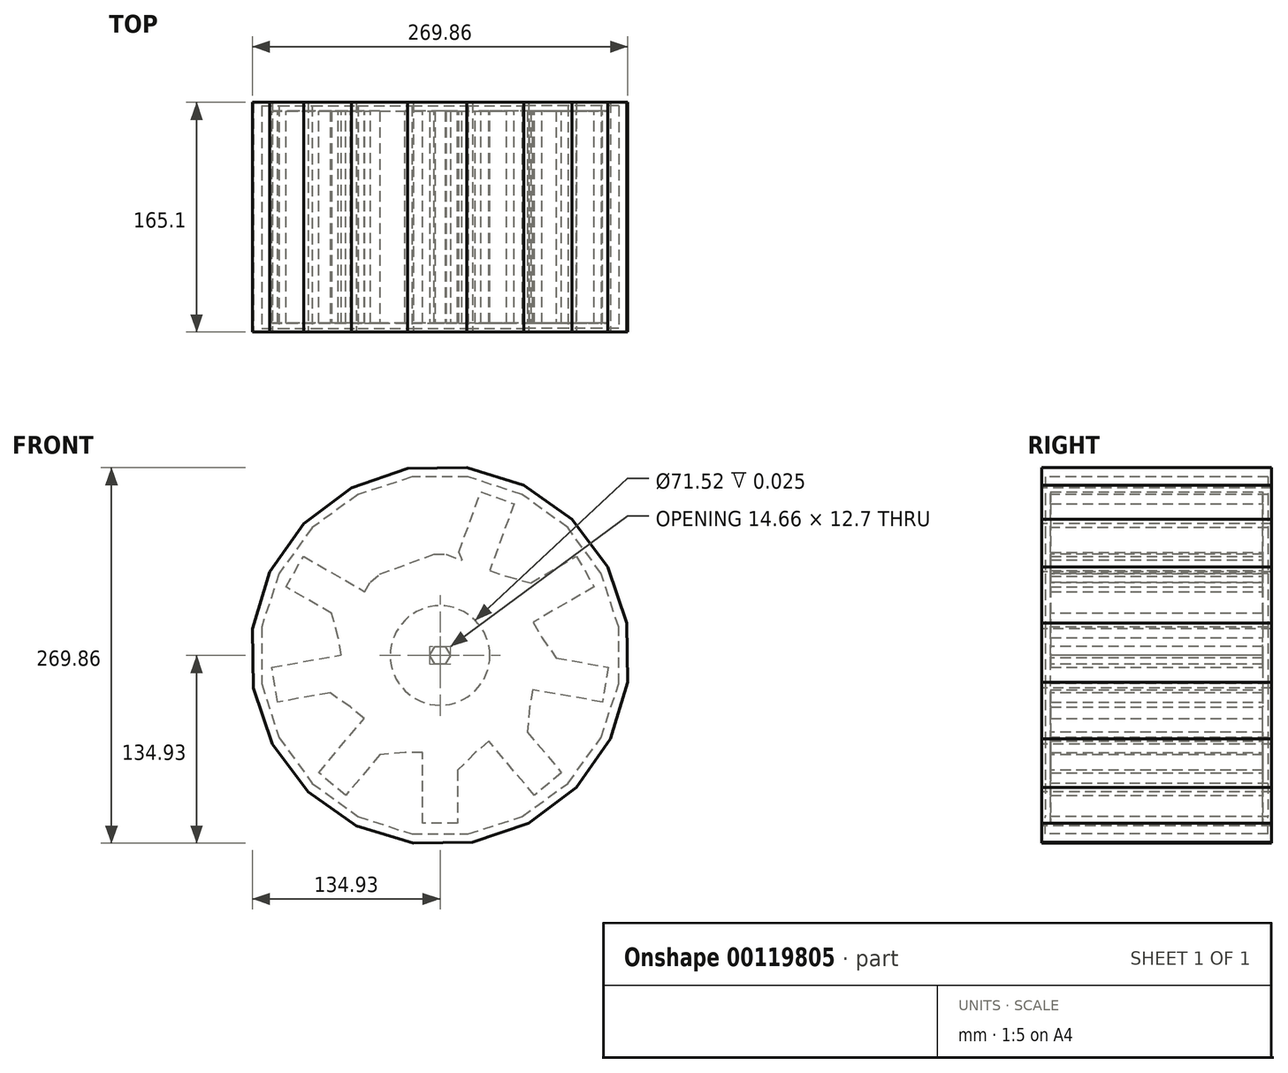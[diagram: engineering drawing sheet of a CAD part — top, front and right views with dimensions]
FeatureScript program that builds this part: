
annotation { "Feature Type Name" : "Feature", "Feature Type Description" : "" }
export const myFeature = defineFeature(function(context is Context, id is Id, definition is map)
    precondition{}
    {
        {
            var Q0;
            Q0=qCreatedBy(makeId("Front.planeOp"),FACE);
            var sketch = newSketch(context, id + "F0", { "sketchPlane" : qUnion([Q0])});
            skCircle(sketch, "E0.cCircle", {"center": v(0, 0) * mm, "radius": 69.79 * mm, "construction": true});
            skLineSegment(sketch, "E0.0", {"start": v(25.4, -69.79) * mm, "end": v(-25.4, -69.79) * mm});
            skLineSegment(sketch, "E0.1", {"start": v(-25.4, -69.79) * mm, "end": v(-64.32, -37.13) * mm});
            skLineSegment(sketch, "E0.2", {"start": v(-64.32, -37.13) * mm, "end": v(-73.14, 12.9) * mm});
            skLineSegment(sketch, "E0.3", {"start": v(-73.14, 12.9) * mm, "end": v(-47.74, 56.9) * mm});
            skLineSegment(sketch, "E0.4", {"start": v(-47.74, 56.9) * mm, "end": v(0, 74.26) * mm});
            skLineSegment(sketch, "E0.5", {"start": v(0, 74.26) * mm, "end": v(47.74, 56.9) * mm});
            skLineSegment(sketch, "E0.6", {"start": v(47.74, 56.9) * mm, "end": v(73.14, 12.9) * mm});
            skLineSegment(sketch, "E0.7", {"start": v(73.14, 12.9) * mm, "end": v(64.32, -37.13) * mm});
            skLineSegment(sketch, "E0.8", {"start": v(64.32, -37.13) * mm, "end": v(25.4, -69.79) * mm});
            skPoint(sketch, "E0.0.midPoint", {"position": v(0, -69.79) * mm});
            skLineSegment(sketch, "E1", {"start": v(-66.79, 23.9) * mm, "end": v(-110.78, 49.3) * mm});
            skLineSegment(sketch, "E2", {"start": v(-110.78, 49.3) * mm, "end": v(-98.08, 71.3) * mm});
            skLineSegment(sketch, "E3", {"start": v(-98.08, 71.3) * mm, "end": v(-54.09, 45.9) * mm});
            skLineSegment(sketch, "E4", {"start": v(-11.93, 69.92) * mm, "end": v(-29.3, 117.66) * mm});
            skLineSegment(sketch, "E5", {"start": v(-29.3, 117.66) * mm, "end": v(-5.44, 126.34) * mm});
            skLineSegment(sketch, "E6", {"start": v(-5.44, 126.34) * mm, "end": v(15.8, 67.97) * mm});
            skLineSegment(sketch, "E7.1.0", {"start": v(-120.96, -8.43) * mm, "end": v(-70.93, 0.39) * mm});
            skLineSegment(sketch, "E7.1.1", {"start": v(-66.52, -24.63) * mm, "end": v(-116.55, -33.45) * mm});
            skLineSegment(sketch, "E7.1.2", {"start": v(-116.55, -33.45) * mm, "end": v(-120.96, -8.43) * mm});
            skLineSegment(sketch, "E7.2.0", {"start": v(-87.24, -84.21) * mm, "end": v(-54.59, -45.3) * mm});
            skLineSegment(sketch, "E7.2.1", {"start": v(-35.13, -61.62) * mm, "end": v(-67.78, -100.54) * mm});
            skLineSegment(sketch, "E7.2.2", {"start": v(-67.78, -100.54) * mm, "end": v(-87.24, -84.21) * mm});
            skLineSegment(sketch, "E7.3.0", {"start": v(-12.7, -120.59) * mm, "end": v(-12.7, -69.79) * mm});
            skLineSegment(sketch, "E7.3.1", {"start": v(12.7, -69.79) * mm, "end": v(12.7, -120.59) * mm});
            skLineSegment(sketch, "E7.3.2", {"start": v(12.7, -120.59) * mm, "end": v(-12.7, -120.59) * mm});
            skLineSegment(sketch, "E7.4.0", {"start": v(67.78, -100.54) * mm, "end": v(35.13, -61.62) * mm});
            skLineSegment(sketch, "E7.4.1", {"start": v(54.59, -45.3) * mm, "end": v(87.24, -84.21) * mm});
            skLineSegment(sketch, "E7.4.2", {"start": v(87.24, -84.21) * mm, "end": v(67.78, -100.54) * mm});
            skLineSegment(sketch, "E7.5.0", {"start": v(116.55, -33.45) * mm, "end": v(66.52, -24.63) * mm});
            skLineSegment(sketch, "E7.5.1", {"start": v(70.93, 0.39) * mm, "end": v(120.96, -8.43) * mm});
            skLineSegment(sketch, "E7.5.2", {"start": v(120.96, -8.43) * mm, "end": v(116.55, -33.45) * mm});
            skLineSegment(sketch, "E7.6.0", {"start": v(110.78, 49.3) * mm, "end": v(66.79, 23.9) * mm});
            skLineSegment(sketch, "E7.6.1", {"start": v(54.09, 45.9) * mm, "end": v(98.08, 71.3) * mm});
            skLineSegment(sketch, "E7.6.2", {"start": v(98.08, 71.3) * mm, "end": v(110.78, 49.3) * mm});
            skLineSegment(sketch, "E7.7.0", {"start": v(53.18, 108.97) * mm, "end": v(35.8, 61.23) * mm});
            skLineSegment(sketch, "E7.7.1", {"start": v(11.93, 69.92) * mm, "end": v(29.3, 117.66) * mm});
            skLineSegment(sketch, "E7.7.2", {"start": v(29.3, 117.66) * mm, "end": v(53.18, 108.97) * mm});
            skLineSegment(sketch, "E7.8.0", {"start": v(-29.3, 117.66) * mm, "end": v(-11.93, 69.92) * mm});
            skLineSegment(sketch, "E7.8.1", {"start": v(-35.8, 61.23) * mm, "end": v(-53.18, 108.97) * mm});
            skLineSegment(sketch, "E7.8.2", {"start": v(-53.18, 108.97) * mm, "end": v(-29.3, 117.66) * mm});
            skSolve(sketch);
        }
        {
            var Q0;
            {var subQ20=sQuery(id+"F0.wireOp",EDGE,"E0.8");var subQ23=sQuery(id+"F0.wireOp",EDGE,"E0.0");var subQ33=makeQuery(id+"F0.imprint","INTERSECT",VERTEX,{"derivedFrom":[subQ23,subQ20]});Q0=makeQuery(id+"F0.imprint","IMPRINT",FACE,{"disambiguationData":[TD([[makeQuery(id+"F0.imprint","IMPRINT",EDGE,{"disambiguationData":[TD([[subQ33,-1.0]])],"derivedFrom":subQ23}),-1.0]])]});}
            var Q1;
            {var subQ0=sQuery(id+"F0.wireOp",EDGE,"E1");Q1=makeQuery(id+"F0.imprint","IMPRINT",FACE,{"disambiguationData":[TD([[makeQuery(id+"F0.imprint","IMPRINT",EDGE,{"derivedFrom":subQ0}),-1.0]])]});}
            var Q2;
            {var subQ0=sQuery(id+"F0.wireOp",EDGE,"E7.8.0");Q2=makeQuery(id+"F0.imprint","IMPRINT",FACE,{"disambiguationData":[TD([[makeQuery(id+"F0.imprint","IMPRINT",EDGE,{"derivedFrom":subQ0}),-1.0]])]});}
            var Q3;
            {var subQ0=sQuery(id+"F0.wireOp",EDGE,"E7.7.0");Q3=makeQuery(id+"F0.imprint","IMPRINT",FACE,{"disambiguationData":[TD([[makeQuery(id+"F0.imprint","IMPRINT",EDGE,{"derivedFrom":subQ0}),-1.0]])]});}
            var Q4;
            {var subQ0=sQuery(id+"F0.wireOp",EDGE,"E7.6.0");Q4=makeQuery(id+"F0.imprint","IMPRINT",FACE,{"disambiguationData":[TD([[makeQuery(id+"F0.imprint","IMPRINT",EDGE,{"derivedFrom":subQ0}),-1.0]])]});}
            var Q5;
            {var subQ0=sQuery(id+"F0.wireOp",EDGE,"E7.5.0");Q5=makeQuery(id+"F0.imprint","IMPRINT",FACE,{"disambiguationData":[TD([[makeQuery(id+"F0.imprint","IMPRINT",EDGE,{"derivedFrom":subQ0}),-1.0]])]});}
            var Q6;
            {var subQ0=sQuery(id+"F0.wireOp",EDGE,"E7.4.0");Q6=makeQuery(id+"F0.imprint","IMPRINT",FACE,{"disambiguationData":[TD([[makeQuery(id+"F0.imprint","IMPRINT",EDGE,{"derivedFrom":subQ0}),-1.0]])]});}
            var Q7;
            {var subQ0=sQuery(id+"F0.wireOp",EDGE,"E7.3.0");Q7=makeQuery(id+"F0.imprint","IMPRINT",FACE,{"disambiguationData":[TD([[makeQuery(id+"F0.imprint","IMPRINT",EDGE,{"derivedFrom":subQ0}),-1.0]])]});}
            var Q8;
            {var subQ0=sQuery(id+"F0.wireOp",EDGE,"E7.2.0");Q8=makeQuery(id+"F0.imprint","IMPRINT",FACE,{"disambiguationData":[TD([[makeQuery(id+"F0.imprint","IMPRINT",EDGE,{"derivedFrom":subQ0}),-1.0]])]});}
            var Q9;
            {var subQ0=sQuery(id+"F0.wireOp",EDGE,"E7.1.0");Q9=makeQuery(id+"F0.imprint","IMPRINT",FACE,{"disambiguationData":[TD([[makeQuery(id+"F0.imprint","IMPRINT",EDGE,{"derivedFrom":subQ0}),-1.0]])]});}
            extrude(context, id + "F1", {"entities" : qUnion([Q0, Q1, Q2, Q3, Q4, Q5, Q6, Q7, Q8, Q9]), "depth" : 152.4 * mm});
        }
        {
            var Q0;
            Q0=makeQuery(id+"F1.opExtrude","SWEPT_EDGE",EDGE,{"disambiguationData":[OSD([sQuery(id+"F0.wireOp",EDGE,"E0.6"),sQuery(id+"F0.wireOp",EDGE,"E7.6.1")])]});
            var Q1;
            Q1=makeQuery(id+"F1.opExtrude","SWEPT_EDGE",EDGE,{"disambiguationData":[OSD([sQuery(id+"F0.wireOp",EDGE,"E0.0"),sQuery(id+"F0.wireOp",EDGE,"E7.3.1")])]});
            var Q2;
            Q2=makeQuery(id+"F1.opExtrude","SWEPT_EDGE",EDGE,{"disambiguationData":[OSD([sQuery(id+"F0.wireOp",EDGE,"E0.3"),sQuery(id+"F0.wireOp",EDGE,"E1")])]});
            var Q3;
            Q3=makeQuery(id+"F1.opExtrude","SWEPT_EDGE",EDGE,{"disambiguationData":[OSD([sQuery(id+"F0.wireOp",EDGE,"E0.8"),sQuery(id+"F0.wireOp",EDGE,"E7.4.1")])]});
            var Q4;
            Q4=makeQuery(id+"F1.opExtrude","SWEPT_EDGE",EDGE,{"disambiguationData":[OSD([sQuery(id+"F0.wireOp",EDGE,"E0.4"),sQuery(id+"F0.wireOp",EDGE,"E7.8.1")])]});
            var Q5;
            Q5=makeQuery(id+"F1.opExtrude","SWEPT_EDGE",EDGE,{"disambiguationData":[OSD([sQuery(id+"F0.wireOp",EDGE,"E0.2"),sQuery(id+"F0.wireOp",EDGE,"E7.1.1")])]});
            var Q6;
            Q6=makeQuery(id+"F1.opExtrude","SWEPT_EDGE",EDGE,{"disambiguationData":[OSD([sQuery(id+"F0.wireOp",EDGE,"E0.7"),sQuery(id+"F0.wireOp",EDGE,"E7.5.1")])]});
            var Q7;
            Q7=makeQuery(id+"F1.opExtrude","SWEPT_EDGE",EDGE,{"disambiguationData":[OSD([sQuery(id+"F0.wireOp",EDGE,"E0.1"),sQuery(id+"F0.wireOp",EDGE,"E7.2.1")])]});
            chamfer(context, id + "F2", {"entities" : qUnion([Q0, Q1, Q2, Q3, Q4, Q5, Q6, Q7]), "width" : 12.7 * mm, "tangentPropagation" : true});
        }
        {
            var Q0;
            Q0=makeQuery(id+"F1.opExtrude","CAP_FACE",FACE,{"disambiguationData":[OSD([sQuery(id+"F0.wireOp",EDGE,"E0.0"),sQuery(id+"F0.wireOp",EDGE,"E0.1"),sQuery(id+"F0.wireOp",EDGE,"E0.2"),sQuery(id+"F0.wireOp",EDGE,"E0.3"),sQuery(id+"F0.wireOp",EDGE,"E0.4"),sQuery(id+"F0.wireOp",EDGE,"E0.5"),sQuery(id+"F0.wireOp",EDGE,"E0.6"),sQuery(id+"F0.wireOp",EDGE,"E0.7"),sQuery(id+"F0.wireOp",EDGE,"E0.8"),sQuery(id+"F0.wireOp",EDGE,"E1"),sQuery(id+"F0.wireOp",EDGE,"E2"),sQuery(id+"F0.wireOp",EDGE,"E3"),sQuery(id+"F0.wireOp",EDGE,"E7.1.0"),sQuery(id+"F0.wireOp",EDGE,"E7.1.1"),sQuery(id+"F0.wireOp",EDGE,"E7.1.2"),sQuery(id+"F0.wireOp",EDGE,"E7.2.0"),sQuery(id+"F0.wireOp",EDGE,"E7.2.1"),sQuery(id+"F0.wireOp",EDGE,"E7.2.2"),sQuery(id+"F0.wireOp",EDGE,"E7.3.0"),sQuery(id+"F0.wireOp",EDGE,"E7.3.1"),sQuery(id+"F0.wireOp",EDGE,"E7.3.2"),sQuery(id+"F0.wireOp",EDGE,"E7.4.0"),sQuery(id+"F0.wireOp",EDGE,"E7.4.1"),sQuery(id+"F0.wireOp",EDGE,"E7.4.2"),sQuery(id+"F0.wireOp",EDGE,"E7.5.0"),sQuery(id+"F0.wireOp",EDGE,"E7.5.1"),sQuery(id+"F0.wireOp",EDGE,"E7.5.2"),sQuery(id+"F0.wireOp",EDGE,"E7.6.0"),sQuery(id+"F0.wireOp",EDGE,"E7.6.1"),sQuery(id+"F0.wireOp",EDGE,"E7.6.2"),sQuery(id+"F0.wireOp",EDGE,"E7.7.0"),sQuery(id+"F0.wireOp",EDGE,"E7.7.1"),sQuery(id+"F0.wireOp",EDGE,"E7.7.2"),sQuery(id+"F0.wireOp",EDGE,"E7.8.0"),sQuery(id+"F0.wireOp",EDGE,"E7.8.1"),sQuery(id+"F0.wireOp",EDGE,"E7.8.2")])],"isStart":false});
            var sketch = newSketch(context, id + "F3", { "sketchPlane" : qUnion([Q0])});
            skCircle(sketch, "E8.cCircle", {"center": v(0, 0) * mm, "radius": 6.35 * mm, "construction": true});
            skLineSegment(sketch, "E8.0", {"start": v(3.67, -6.35) * mm, "end": v(-3.67, -6.35) * mm});
            skLineSegment(sketch, "E8.1", {"start": v(-3.67, -6.35) * mm, "end": v(-7.33, 0) * mm});
            skLineSegment(sketch, "E8.2", {"start": v(-7.33, 0) * mm, "end": v(-3.67, 6.35) * mm});
            skLineSegment(sketch, "E8.3", {"start": v(-3.67, 6.35) * mm, "end": v(3.67, 6.35) * mm});
            skLineSegment(sketch, "E8.4", {"start": v(3.67, 6.35) * mm, "end": v(7.33, 0) * mm});
            skLineSegment(sketch, "E8.5", {"start": v(7.33, 0) * mm, "end": v(3.67, -6.35) * mm});
            skPoint(sketch, "E8.0.midPoint", {"position": v(0, -6.35) * mm});
            skSolve(sketch);
        }
        {
            var Q0;
            Q0 = qSketchRegion(id + "F3", true);
            extrude(context, id + "F4", {"entities" : qUnion([Q0]), "operationType" : NewBodyOperationType.REMOVE, "endBound" : BoundingType.THROUGH_ALL, "oppositeDirection" : true, "depth" : 25.4 * mm});
        }
        {
            var Q0;
            Q0=makeQuery(id+"F1.opExtrude","CAP_FACE",FACE,{"disambiguationData":[OSD([sQuery(id+"F0.wireOp",EDGE,"E0.0"),sQuery(id+"F0.wireOp",EDGE,"E0.1"),sQuery(id+"F0.wireOp",EDGE,"E0.2"),sQuery(id+"F0.wireOp",EDGE,"E0.3"),sQuery(id+"F0.wireOp",EDGE,"E0.4"),sQuery(id+"F0.wireOp",EDGE,"E0.5"),sQuery(id+"F0.wireOp",EDGE,"E0.6"),sQuery(id+"F0.wireOp",EDGE,"E0.7"),sQuery(id+"F0.wireOp",EDGE,"E0.8"),sQuery(id+"F0.wireOp",EDGE,"E1"),sQuery(id+"F0.wireOp",EDGE,"E2"),sQuery(id+"F0.wireOp",EDGE,"E3"),sQuery(id+"F0.wireOp",EDGE,"E6"),sQuery(id+"F0.wireOp",EDGE,"E7.1.0"),sQuery(id+"F0.wireOp",EDGE,"E7.1.1"),sQuery(id+"F0.wireOp",EDGE,"E7.1.2"),sQuery(id+"F0.wireOp",EDGE,"E7.2.0"),sQuery(id+"F0.wireOp",EDGE,"E7.2.1"),sQuery(id+"F0.wireOp",EDGE,"E7.2.2"),sQuery(id+"F0.wireOp",EDGE,"E7.3.0"),sQuery(id+"F0.wireOp",EDGE,"E7.3.1"),sQuery(id+"F0.wireOp",EDGE,"E7.3.2"),sQuery(id+"F0.wireOp",EDGE,"E7.4.0"),sQuery(id+"F0.wireOp",EDGE,"E7.4.1"),sQuery(id+"F0.wireOp",EDGE,"E7.4.2"),sQuery(id+"F0.wireOp",EDGE,"E7.5.0"),sQuery(id+"F0.wireOp",EDGE,"E7.5.1"),sQuery(id+"F0.wireOp",EDGE,"E7.5.2"),sQuery(id+"F0.wireOp",EDGE,"E7.6.0"),sQuery(id+"F0.wireOp",EDGE,"E7.6.1"),sQuery(id+"F0.wireOp",EDGE,"E7.6.2"),sQuery(id+"F0.wireOp",EDGE,"E7.7.0"),sQuery(id+"F0.wireOp",EDGE,"E7.7.1"),sQuery(id+"F0.wireOp",EDGE,"E7.7.2"),sQuery(id+"F0.wireOp",EDGE,"E7.8.0"),sQuery(id+"F0.wireOp",EDGE,"E7.8.1"),sQuery(id+"F0.wireOp",EDGE,"E7.8.2")])],"isStart":false});
            var sketch = newSketch(context, id + "F5", { "sketchPlane" : qUnion([Q0])});
            skCircle(sketch, "E9.cCircle", {"center": v(0, 0) * mm, "radius": 128.27 * mm, "construction": true});
            skLineSegment(sketch, "E9.0", {"start": v(20.32, -128.27) * mm, "end": v(-20.32, -128.27) * mm});
            skLineSegment(sketch, "E9.1", {"start": v(-20.32, -128.27) * mm, "end": v(-58.96, -115.71) * mm});
            skLineSegment(sketch, "E9.2", {"start": v(-58.96, -115.71) * mm, "end": v(-91.83, -91.83) * mm});
            skLineSegment(sketch, "E9.3", {"start": v(-91.83, -91.83) * mm, "end": v(-115.71, -58.96) * mm});
            skLineSegment(sketch, "E9.4", {"start": v(-115.71, -58.96) * mm, "end": v(-128.27, -20.32) * mm});
            skLineSegment(sketch, "E9.5", {"start": v(-128.27, -20.32) * mm, "end": v(-128.27, 20.32) * mm});
            skLineSegment(sketch, "E9.6", {"start": v(-128.27, 20.32) * mm, "end": v(-115.71, 58.96) * mm});
            skLineSegment(sketch, "E9.7", {"start": v(-115.71, 58.96) * mm, "end": v(-91.83, 91.83) * mm});
            skLineSegment(sketch, "E9.8", {"start": v(-91.83, 91.83) * mm, "end": v(-58.96, 115.71) * mm});
            skLineSegment(sketch, "E9.9", {"start": v(-58.96, 115.71) * mm, "end": v(-20.32, 128.27) * mm});
            skLineSegment(sketch, "E9.10", {"start": v(-20.32, 128.27) * mm, "end": v(20.32, 128.27) * mm});
            skLineSegment(sketch, "E9.11", {"start": v(20.32, 128.27) * mm, "end": v(58.96, 115.71) * mm});
            skLineSegment(sketch, "E9.12", {"start": v(58.96, 115.71) * mm, "end": v(91.83, 91.83) * mm});
            skLineSegment(sketch, "E9.13", {"start": v(91.83, 91.83) * mm, "end": v(115.71, 58.96) * mm});
            skLineSegment(sketch, "E9.14", {"start": v(115.71, 58.96) * mm, "end": v(128.27, 20.32) * mm});
            skLineSegment(sketch, "E9.15", {"start": v(128.27, 20.32) * mm, "end": v(128.27, -20.32) * mm});
            skLineSegment(sketch, "E9.16", {"start": v(128.27, -20.32) * mm, "end": v(115.71, -58.96) * mm});
            skLineSegment(sketch, "E9.17", {"start": v(115.71, -58.96) * mm, "end": v(91.83, -91.83) * mm});
            skLineSegment(sketch, "E9.18", {"start": v(91.83, -91.83) * mm, "end": v(58.96, -115.71) * mm});
            skLineSegment(sketch, "E9.19", {"start": v(58.96, -115.71) * mm, "end": v(20.32, -128.27) * mm});
            skPoint(sketch, "E9.0.midPoint", {"position": v(0, -128.27) * mm});
            skCircle(sketch, "E10.cCircle", {"center": v(0, 0) * mm, "radius": 134.62 * mm, "construction": true});
            skPoint(sketch, "E10.cCircle.perimeterSnap0", {"position": v(-122, 39.64) * mm});
            skLineSegment(sketch, "E10.0", {"start": v(-134.93, 19.26) * mm, "end": v(-122.37, 60.01) * mm});
            skLineSegment(sketch, "E10.1", {"start": v(-122.37, 60.01) * mm, "end": v(-97.84, 94.9) * mm});
            skLineSegment(sketch, "E10.2", {"start": v(-97.84, 94.9) * mm, "end": v(-63.73, 120.48) * mm});
            skLineSegment(sketch, "E10.3", {"start": v(-63.73, 120.48) * mm, "end": v(-23.38, 134.28) * mm});
            skLineSegment(sketch, "E10.4", {"start": v(-23.38, 134.28) * mm, "end": v(19.26, 134.93) * mm});
            skLineSegment(sketch, "E10.5", {"start": v(19.26, 134.93) * mm, "end": v(60.01, 122.37) * mm});
            skLineSegment(sketch, "E10.6", {"start": v(60.01, 122.37) * mm, "end": v(94.9, 97.84) * mm});
            skLineSegment(sketch, "E10.7", {"start": v(94.9, 97.84) * mm, "end": v(120.48, 63.73) * mm});
            skLineSegment(sketch, "E10.8", {"start": v(120.48, 63.73) * mm, "end": v(134.28, 23.38) * mm});
            skLineSegment(sketch, "E10.9", {"start": v(134.28, 23.38) * mm, "end": v(134.93, -19.26) * mm});
            skLineSegment(sketch, "E10.10", {"start": v(134.93, -19.26) * mm, "end": v(122.37, -60.01) * mm});
            skLineSegment(sketch, "E10.11", {"start": v(122.37, -60.01) * mm, "end": v(97.84, -94.9) * mm});
            skLineSegment(sketch, "E10.12", {"start": v(97.84, -94.9) * mm, "end": v(63.73, -120.48) * mm});
            skLineSegment(sketch, "E10.13", {"start": v(63.73, -120.48) * mm, "end": v(23.38, -134.28) * mm});
            skLineSegment(sketch, "E10.14", {"start": v(23.38, -134.28) * mm, "end": v(-19.26, -134.93) * mm});
            skLineSegment(sketch, "E10.15", {"start": v(-19.26, -134.93) * mm, "end": v(-60.01, -122.37) * mm});
            skLineSegment(sketch, "E10.16", {"start": v(-60.01, -122.37) * mm, "end": v(-94.9, -97.84) * mm});
            skLineSegment(sketch, "E10.17", {"start": v(-94.9, -97.84) * mm, "end": v(-120.48, -63.73) * mm});
            skLineSegment(sketch, "E10.18", {"start": v(-120.48, -63.73) * mm, "end": v(-134.28, -23.38) * mm});
            skLineSegment(sketch, "E10.19", {"start": v(-134.28, -23.38) * mm, "end": v(-134.93, 19.26) * mm});
            skPoint(sketch, "E10.0.midPoint", {"position": v(-128.65, 39.64) * mm});
            skPoint(sketch, "E10.0.midPoint.positionSnap0", {"position": v(-122, 39.64) * mm});
            skSolve(sketch);
        }
        {
            var Q0;
            Q0 = qSketchRegion(id + "F5", true);
            extrude(context, id + "F6", {"entities" : qUnion([Q0]), "oppositeDirection" : true, "depth" : 158.75 * mm, "hasSecondDirection" : true, "secondDirectionOppositeDirection" : false, "secondDirectionDepth" : 6.35 * mm});
        }
        {
            var Q0;
            Q0=makeQuery(id+"F6.opExtrude","CAP_FACE",FACE,{"disambiguationData":[OSD([sQuery(id+"F5.wireOp",EDGE,"E9.0"),sQuery(id+"F5.wireOp",EDGE,"E9.1"),sQuery(id+"F5.wireOp",EDGE,"E9.2"),sQuery(id+"F5.wireOp",EDGE,"E9.3"),sQuery(id+"F5.wireOp",EDGE,"E9.4"),sQuery(id+"F5.wireOp",EDGE,"E9.5"),sQuery(id+"F5.wireOp",EDGE,"E9.6"),sQuery(id+"F5.wireOp",EDGE,"E9.7"),sQuery(id+"F5.wireOp",EDGE,"E9.8"),sQuery(id+"F5.wireOp",EDGE,"E9.9"),sQuery(id+"F5.wireOp",EDGE,"E9.10"),sQuery(id+"F5.wireOp",EDGE,"E9.11"),sQuery(id+"F5.wireOp",EDGE,"E9.12"),sQuery(id+"F5.wireOp",EDGE,"E9.13"),sQuery(id+"F5.wireOp",EDGE,"E9.14"),sQuery(id+"F5.wireOp",EDGE,"E9.15"),sQuery(id+"F5.wireOp",EDGE,"E9.16"),sQuery(id+"F5.wireOp",EDGE,"E9.17"),sQuery(id+"F5.wireOp",EDGE,"E9.18"),sQuery(id+"F5.wireOp",EDGE,"E9.19"),sQuery(id+"F5.wireOp",EDGE,"E10.0"),sQuery(id+"F5.wireOp",EDGE,"E10.1"),sQuery(id+"F5.wireOp",EDGE,"E10.2"),sQuery(id+"F5.wireOp",EDGE,"E10.3"),sQuery(id+"F5.wireOp",EDGE,"E10.4"),sQuery(id+"F5.wireOp",EDGE,"E10.5"),sQuery(id+"F5.wireOp",EDGE,"E10.6"),sQuery(id+"F5.wireOp",EDGE,"E10.7"),sQuery(id+"F5.wireOp",EDGE,"E10.8"),sQuery(id+"F5.wireOp",EDGE,"E10.9"),sQuery(id+"F5.wireOp",EDGE,"E10.10"),sQuery(id+"F5.wireOp",EDGE,"E10.11"),sQuery(id+"F5.wireOp",EDGE,"E10.12"),sQuery(id+"F5.wireOp",EDGE,"E10.13"),sQuery(id+"F5.wireOp",EDGE,"E10.14"),sQuery(id+"F5.wireOp",EDGE,"E10.15"),sQuery(id+"F5.wireOp",EDGE,"E10.16"),sQuery(id+"F5.wireOp",EDGE,"E10.17"),sQuery(id+"F5.wireOp",EDGE,"E10.18"),sQuery(id+"F5.wireOp",EDGE,"E10.19")])],"isStart":true});
            var sketch = newSketch(context, id + "F7", { "sketchPlane" : qUnion([Q0])});
            skCircle(sketch, "E11", {"center": v(0, 0) * mm, "radius": 129.87 * mm});
            skSolve(sketch);
        }
        {
            var Q0;
            Q0 = qSketchRegion(id + "F7", true);
            extrude(context, id + "F8", {"entities" : qUnion([Q0]), "operationType" : NewBodyOperationType.ADD, "oppositeDirection" : true, "depth" : 2.54 * mm});
        }
        {
            var Q0;
            Q0=makeQuery(id+"F6.opExtrude","CAP_FACE",FACE,{"disambiguationData":[OSD([sQuery(id+"F5.wireOp",EDGE,"E9.0"),sQuery(id+"F5.wireOp",EDGE,"E9.1"),sQuery(id+"F5.wireOp",EDGE,"E9.2"),sQuery(id+"F5.wireOp",EDGE,"E9.3"),sQuery(id+"F5.wireOp",EDGE,"E9.4"),sQuery(id+"F5.wireOp",EDGE,"E9.5"),sQuery(id+"F5.wireOp",EDGE,"E9.6"),sQuery(id+"F5.wireOp",EDGE,"E9.7"),sQuery(id+"F5.wireOp",EDGE,"E9.8"),sQuery(id+"F5.wireOp",EDGE,"E9.9"),sQuery(id+"F5.wireOp",EDGE,"E9.10"),sQuery(id+"F5.wireOp",EDGE,"E9.11"),sQuery(id+"F5.wireOp",EDGE,"E9.12"),sQuery(id+"F5.wireOp",EDGE,"E9.13"),sQuery(id+"F5.wireOp",EDGE,"E9.14"),sQuery(id+"F5.wireOp",EDGE,"E9.15"),sQuery(id+"F5.wireOp",EDGE,"E9.16"),sQuery(id+"F5.wireOp",EDGE,"E9.17"),sQuery(id+"F5.wireOp",EDGE,"E9.18"),sQuery(id+"F5.wireOp",EDGE,"E9.19"),sQuery(id+"F5.wireOp",EDGE,"E10.0"),sQuery(id+"F5.wireOp",EDGE,"E10.1"),sQuery(id+"F5.wireOp",EDGE,"E10.2"),sQuery(id+"F5.wireOp",EDGE,"E10.3"),sQuery(id+"F5.wireOp",EDGE,"E10.4"),sQuery(id+"F5.wireOp",EDGE,"E10.5"),sQuery(id+"F5.wireOp",EDGE,"E10.6"),sQuery(id+"F5.wireOp",EDGE,"E10.7"),sQuery(id+"F5.wireOp",EDGE,"E10.8"),sQuery(id+"F5.wireOp",EDGE,"E10.9"),sQuery(id+"F5.wireOp",EDGE,"E10.10"),sQuery(id+"F5.wireOp",EDGE,"E10.11"),sQuery(id+"F5.wireOp",EDGE,"E10.12"),sQuery(id+"F5.wireOp",EDGE,"E10.13"),sQuery(id+"F5.wireOp",EDGE,"E10.14"),sQuery(id+"F5.wireOp",EDGE,"E10.15"),sQuery(id+"F5.wireOp",EDGE,"E10.16"),sQuery(id+"F5.wireOp",EDGE,"E10.17"),sQuery(id+"F5.wireOp",EDGE,"E10.18"),sQuery(id+"F5.wireOp",EDGE,"E10.19")])],"isStart":false});
            var sketch = newSketch(context, id + "F9", { "sketchPlane" : qUnion([Q0])});
            skCircle(sketch, "E12", {"center": v(0, 0) * mm, "radius": 129.87 * mm});
            skSolve(sketch);
        }
        {
            var Q0;
            Q0 = qSketchRegion(id + "F9", true);
            extrude(context, id + "F10", {"entities" : qUnion([Q0]), "operationType" : NewBodyOperationType.ADD, "oppositeDirection" : true, "depth" : 2.54 * mm});
        }
        {
            var Q0;
            Q0=makeQuery(id+"F10.boolean.opBoolean","MERGE",FACE,{"derivedFrom":[makeQuery(id+"F6.opExtrude","CAP_FACE",FACE,{"disambiguationData":[OSD([sQuery(id+"F5.wireOp",EDGE,"E9.0"),sQuery(id+"F5.wireOp",EDGE,"E9.1"),sQuery(id+"F5.wireOp",EDGE,"E9.2"),sQuery(id+"F5.wireOp",EDGE,"E9.3"),sQuery(id+"F5.wireOp",EDGE,"E9.4"),sQuery(id+"F5.wireOp",EDGE,"E9.5"),sQuery(id+"F5.wireOp",EDGE,"E9.6"),sQuery(id+"F5.wireOp",EDGE,"E9.7"),sQuery(id+"F5.wireOp",EDGE,"E9.8"),sQuery(id+"F5.wireOp",EDGE,"E9.9"),sQuery(id+"F5.wireOp",EDGE,"E9.10"),sQuery(id+"F5.wireOp",EDGE,"E9.11"),sQuery(id+"F5.wireOp",EDGE,"E9.12"),sQuery(id+"F5.wireOp",EDGE,"E9.13"),sQuery(id+"F5.wireOp",EDGE,"E9.14"),sQuery(id+"F5.wireOp",EDGE,"E9.15"),sQuery(id+"F5.wireOp",EDGE,"E9.16"),sQuery(id+"F5.wireOp",EDGE,"E9.17"),sQuery(id+"F5.wireOp",EDGE,"E9.18"),sQuery(id+"F5.wireOp",EDGE,"E9.19"),sQuery(id+"F5.wireOp",EDGE,"E10.0"),sQuery(id+"F5.wireOp",EDGE,"E10.1"),sQuery(id+"F5.wireOp",EDGE,"E10.2"),sQuery(id+"F5.wireOp",EDGE,"E10.3"),sQuery(id+"F5.wireOp",EDGE,"E10.4"),sQuery(id+"F5.wireOp",EDGE,"E10.5"),sQuery(id+"F5.wireOp",EDGE,"E10.6"),sQuery(id+"F5.wireOp",EDGE,"E10.7"),sQuery(id+"F5.wireOp",EDGE,"E10.8"),sQuery(id+"F5.wireOp",EDGE,"E10.9"),sQuery(id+"F5.wireOp",EDGE,"E10.10"),sQuery(id+"F5.wireOp",EDGE,"E10.11"),sQuery(id+"F5.wireOp",EDGE,"E10.12"),sQuery(id+"F5.wireOp",EDGE,"E10.13"),sQuery(id+"F5.wireOp",EDGE,"E10.14"),sQuery(id+"F5.wireOp",EDGE,"E10.15"),sQuery(id+"F5.wireOp",EDGE,"E10.16"),sQuery(id+"F5.wireOp",EDGE,"E10.17"),sQuery(id+"F5.wireOp",EDGE,"E10.18"),sQuery(id+"F5.wireOp",EDGE,"E10.19")])],"isStart":false}),makeQuery(id+"F10.opExtrude","CAP_FACE",FACE,{"disambiguationData":[OSD([sQuery(id+"F9.wireOp",EDGE,"E12")])],"isStart":true})]});
            var sketch = newSketch(context, id + "F11", { "sketchPlane" : qUnion([Q0])});
            skCircle(sketch, "E13", {"center": v(0, 0) * mm, "radius": 35.76 * mm});
            skSolve(sketch);
        }
        {
            var Q0;
            Q0 = qSketchRegion(id + "F11", true);
            extrude(context, id + "F12", {"entities" : qUnion([Q0]), "operationType" : NewBodyOperationType.REMOVE, "oppositeDirection" : true, "depth" : 0.03 * mm});
        }
    });
